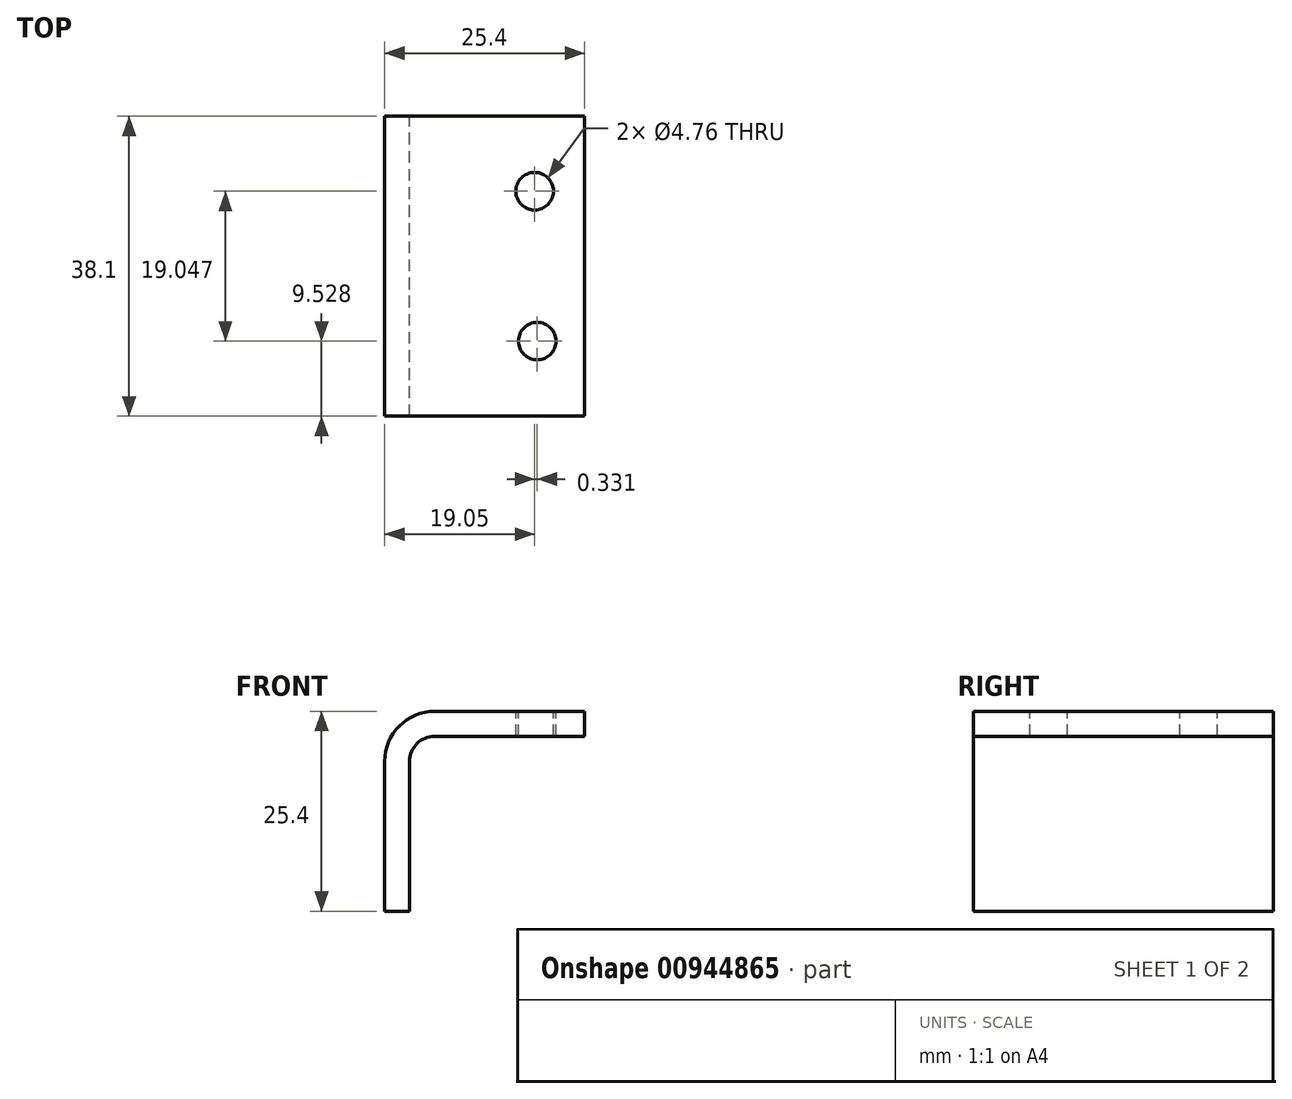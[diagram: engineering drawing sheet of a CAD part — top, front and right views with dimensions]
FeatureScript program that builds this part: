
annotation { "Feature Type Name" : "Feature", "Feature Type Description" : "" }
export const myFeature = defineFeature(function(context is Context, id is Id, definition is map)
    precondition{}
    {
        {
            var Q0;
            Q0=qCreatedBy(makeId("Front.planeOp"),FACE);
            var sketch = newSketch(context, id + "F0", { "sketchPlane" : qUnion([Q0])});
            skLineSegment(sketch, "E0", {"start": v(0, 0) * mm, "end": v(0, 19.05) * mm});
            skLineSegment(sketch, "E1", {"start": v(6.35, 25.4) * mm, "end": v(25.4, 25.4) * mm});
            skLineSegment(sketch, "E2", {"start": v(25.4, 25.4) * mm, "end": v(25.4, 22.23) * mm});
            skLineSegment(sketch, "E3", {"start": v(25.4, 22.23) * mm, "end": v(6.35, 22.22) * mm});
            skLineSegment(sketch, "E4", {"start": v(3.17, 19.05) * mm, "end": v(3.17, 0) * mm});
            skLineSegment(sketch, "E5", {"start": v(3.17, 0) * mm, "end": v(0, 0) * mm});
            skPoint(sketch, "E6.visualSharp", {"position": v(3.17, 22.22) * mm});
            skArc(sketch, "E6.filletArc", {"start": v(6.35, 22.22) * mm, "mid": v(4.1, 21.3) * mm, "end": v(3.17, 19.05) * mm});
            skPoint(sketch, "E7.visualSharp", {"position": v(0, 25.4) * mm});
            skArc(sketch, "E7.filletArc", {"start": v(6.35, 25.4) * mm, "mid": v(1.86, 23.54) * mm, "end": v(0, 19.05) * mm});
            skSolve(sketch);
        }
        {
            var Q0;
            Q0 = qSketchRegion(id + "F0", true);
            extrude(context, id + "F1", {"entities" : qUnion([Q0]), "depth" : 38.1 * mm, "offsetDistance" : 25.4 * mm});
        }
        {
            var Q0;
            Q0=makeQuery(id+"F1.opExtrude","SWEPT_FACE",FACE,{"disambiguationData":[OSD([sQuery(id+"F0.wireOp",EDGE,"E1")])]});
            var sketch = newSketch(context, id + "F2", { "sketchPlane" : qUnion([Q0])});
            skCircle(sketch, "E8", {"center": v(19.05, -9.53) * mm, "radius": 2.38 * mm});
            skCircle(sketch, "E9.0.1.0", {"center": v(19.38, -28.57) * mm, "radius": 2.38 * mm});
            skLineSegment(sketch, "E9.direction1", {"start": v(19.05, -9.53) * mm, "end": v(-6.35, -9.53) * mm, "construction": true});
            skLineSegment(sketch, "E9.direction2", {"start": v(19.05, -9.53) * mm, "end": v(19.38, -28.57) * mm, "construction": true});
            skSolve(sketch);
        }
        {
            var Q0;
            Q0 = qSketchRegion(id + "F2", true);
            extrude(context, id + "F3", {"entities" : qUnion([Q0]), "operationType" : NewBodyOperationType.REMOVE, "oppositeDirection" : true, "depth" : 25.4 * mm, "offsetDistance" : 25.4 * mm});
        }
    });
